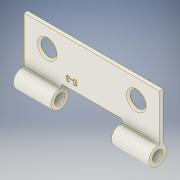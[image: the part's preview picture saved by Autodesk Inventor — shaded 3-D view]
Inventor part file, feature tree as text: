
AUTODESK INVENTOR PART (.ipt)
format: ipt  version: 2017 (Build 210142000, 142)  size: 224,768 bytes
history: native  units: in
note: dims shown in document units (in); Inventor stores cm internally (conversion verified against a paired STEP export)
features: sketch x2, other x1
ambient origin geometry x8: Origin, YZ Plane, XZ Plane, XY Plane, X Axis, Y Axis, Z Axis, Center Point
bodies: Solid1 (feature_tree)
feature tree (3):
  sketch  "Sketch1"
  sketch  "Sketch2"
  other  "Sólido1"
